# Revit family: M751
name_source: partatom
category: Communication Devices
revit_build: Autodesk Revit 2018 (Build: 20170223_1515(x64)
units: mm (PartAtom-declared; Revit-internal decimal feet)

## family parameters
Always vertical = Yes
Cut with Voids When Loaded = No
Maintain Annotation Orientation = No
Part Type = Normal
Room Calculation Point = No
Round Connector Dimension = Use Diameter
Shared = No
Work Plane-Based = No

## types (1)
- M751
    ADDITIONAL FEATURES = AMX Support, Automated Email Alert Function, CEC Support through HDMI, Crestron Roomview Support, Display Browser Control, Display Wall Calibrator Compatible, HDR Support (PQ, HLG, HDR10), Key Guide, NaViSet Administrator 2 Compatible, OSD Rotation for Portrait Orientation, SDM Compatible, PJ Link Support, Powered USB Port (5V/2A), Raspberry Pi Compute Module 4 Compatible, Low Latency Mode, Removeable Logo Ornament, Real Time Clock, Local Dimming, Pivot Feature, G-Sensor, Metal Chassis, New Remote Control Design, Multi Picture Mode (Up to 4 Simultaneous Displays), SpectraView Engine Technology, Quick Input Change, Dual Daisy Chain, Quick Start, Internet Time Server, Auto ID/IP Settings, Energy Star 8.0
    CONNECTIVITY- Input Terminals- Audio = Digital Audio through HDMI x2, Option (SDM), Compute Module and DP x2
    CONNECTIVITY- Input Terminals- Data = USB 2.0 x2 (1x 5V/2A and Service, 1x Downstream Port), USB Type B (Upstream Port and Software)
    CONNECTIVITY- Input Terminals- Digital = HDMI 2.0 x2 (HDMI1 supports ARC), DP 1.4 x2
    CONNECTIVITY- Input Terminals- External Control = LAN (100Mbit), 3.5mm Mini Jack IR Remote, RS-232C
    CONNECTIVITY- Output Terminals- Audio = 3.5mm Mini Jack, External Speaker Jack (15W x 2)
    CONNECTIVITY- Output Terminals- Digital = HDMI x1 (outputs HDMI1, HDMI2 and Option), DisplayPort x1 (Outputs DP1, DP2 and Option**)
    CONNECTIVITY- Output Terminals- External Control = LAN (100Mbit)
    ENVIRONMENTAL CONDITIONS- Operating Altitude = 3000m (9843ft)
    ENVIRONMENTAL CONDITIONS- Operating Humidity = 20-80%
    ENVIRONMENTAL CONDITIONS- Operating Temperature = Integrated and programmable; linked to cooling fans
    LCD MODULE- Aspect Ratio = 16:9
    LCD MODULE- Brightness (Typical/Minimum) = 500 cd/m2
    LCD MODULE- Contrast Ratio (Typical)* = ≥8000:1
    LCD MODULE- Displayable Colors = Over 1.07 Billion (10bit)
    LCD MODULE- Native Resolution = 3840 x 2160
    LCD MODULE- Orientation = Landscape and Portrait (CCW Rotation)
    LCD MODULE- Panel Haze (%) = 28 (Professional)
    LCD MODULE- Viewable Image Size = 75in.
    LCD MODULE- Viewing Angle = 178° Vert., 178° Hor. (89U/89D/89L/89R) @ CR>10
    LIMITED WARRANTY = 3 years Advanced Replacement
    Manufacturer = NEC Display Solutions
    Model = M751
    Optional Speakers = SP-RM3
    Optional Stand = ST-801
    Other Accessories = ATSC/NTSC SDM Tuner (DS1-TM01), All SDM PC's (SDM-VI5W-PS, SDM-VI3W-IS, SDM-VICW-IS), 12G-SDI SDM Module (SDM-12GSDI), HDBaseT SDM Module (SDM-HDBT), SDM Raspberry Pi Compute Module 4 with optional NEC Interface Board (MPi4E or MPi4W), Human Sensor (KT-RC3)
    PHYSICAL SPECS- Bezel Width (L/R, T/B) = 14.3mm/14.3mm/14.3mm/14.8mm
    PHYSICAL SPECS- Net Dimensions (Without stand, W x H x D) = 66.2 x 37.8 x 3.3in. (1682.3 x 961.1 x 83.2mm)
    PHYSICAL SPECS- Net Weight = 38.2kg / 84.2lbs.
    PHYSICAL SPECS- VESA Hole Configuration = 600mm x 400mm
    POWER CONSUMPTION- Current Rating = 4.9A - 2.0A @ 100V - 240V
    POWER CONSUMPTION- Network Standby = 2W
    POWER CONSUMPTION- Normal Standby = 0.5W
    POWER CONSUMPTION- On (Typ/Max Brightness/All Max) = 205W/275W/410W
    POWER CONSUMPTION- Speaker Rating = Integrated 10W x 2, Optional through SP-RM3
    SENSORS- Ambient Light Sensor = Integrated
    SENSORS- Human Sensor = Optional (KT-RC3)
    SENSORS- Temperature Sensor = Integrated and programmable; linked to cooling fans
    SHIPS WITH = 3.0m Power Cable, IR Remote Control, 3.0m HDMI Cable, AAA Batteries x2, Setup Manual
    URL = www.necdisplay.com

## geometry (parser evidence)
native form markers: Sweep x3
no freeform markers — native parametric forms only
